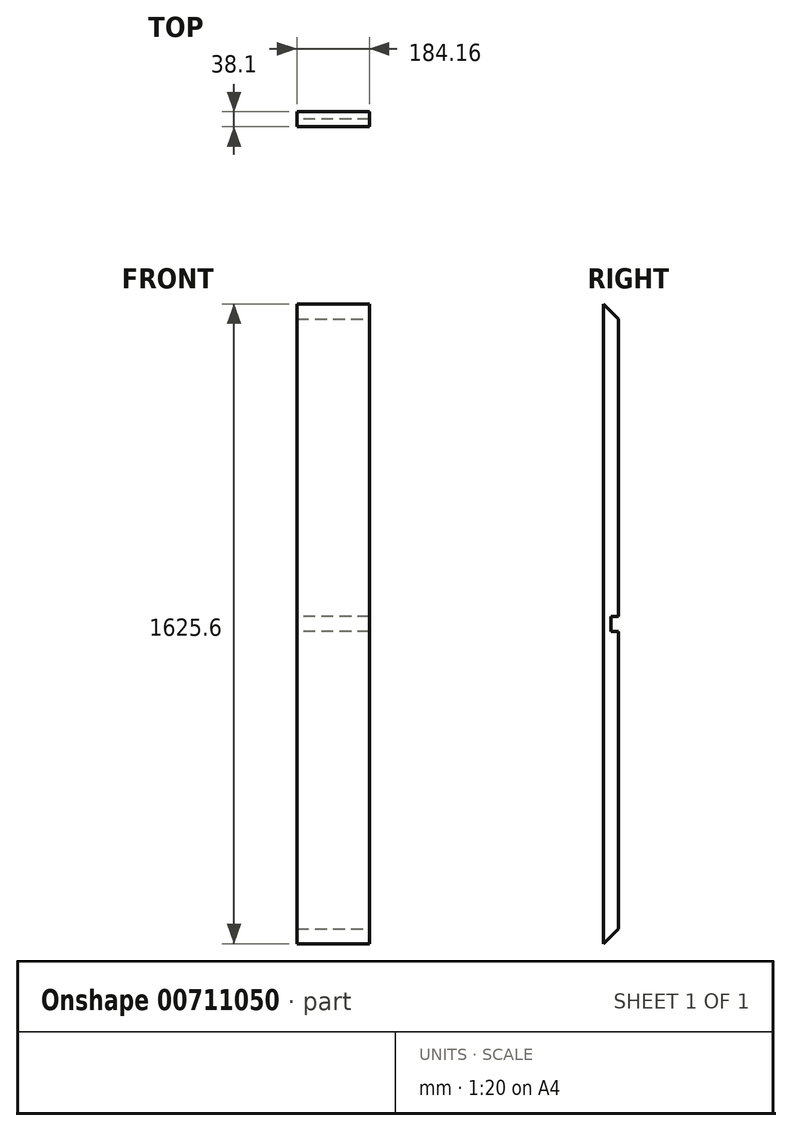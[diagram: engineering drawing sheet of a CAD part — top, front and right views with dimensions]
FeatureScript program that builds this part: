
annotation { "Feature Type Name" : "Feature", "Feature Type Description" : "" }
export const myFeature = defineFeature(function(context is Context, id is Id, definition is map)
    precondition{}
    {
        {
            var Q0;
            Q0=qCreatedBy(makeId("Top.planeOp"),FACE);
            var sketch = newSketch(context, id + "F0", { "sketchPlane" : qUnion([Q0])});
            skLineSegment(sketch, "E0.bottom", {"start": v(92.08, 19.05) * mm, "end": v(-92.08, 19.05) * mm});
            skLineSegment(sketch, "E0.top", {"start": v(92.08, -19.05) * mm, "end": v(-92.07, -19.05) * mm});
            skLineSegment(sketch, "E0.left", {"start": v(92.08, 19.05) * mm, "end": v(92.08, -19.05) * mm});
            skLineSegment(sketch, "E0.right", {"start": v(-92.08, 19.05) * mm, "end": v(-92.08, -19.05) * mm});
            skPoint(sketch, "E0.middle", {"position": v(0, 0) * mm});
            skSolve(sketch);
        }
        {
            var Q0;
            Q0=makeQuery(id+"F0.imprint","IMPRINT",FACE,{"disambiguationData":[TD([[makeQuery(id+"F0.imprint","IMPRINT",EDGE,{"derivedFrom":sQuery(id+"F0.wireOp",EDGE,"E0.bottom")}),1.0]])]});
            extrude(context, id + "F1", {"entities" : qUnion([Q0]), "depth" : 1625.6 * mm, "offsetDistance" : 25.4 * mm});
        }
        {
            var Q0;
            Q0=makeQuery(id+"F1.opExtrude","SWEPT_FACE",FACE,{"disambiguationData":[OSD([sQuery(id+"F0.wireOp",EDGE,"E0.left")])]});
            var sketch = newSketch(context, id + "F2", { "sketchPlane" : qUnion([Q0])});
            skLineSegment(sketch, "E1", {"start": v(-19.05, 1625.6) * mm, "end": v(19.05, 1587.5) * mm});
            skLineSegment(sketch, "E2", {"start": v(-19.05, 1625.6) * mm, "end": v(19.05, 1625.6) * mm});
            skLineSegment(sketch, "E3", {"start": v(19.05, 1625.6) * mm, "end": v(19.05, 1587.5) * mm});
            skLineSegment(sketch, "E4", {"start": v(-19.05, 0) * mm, "end": v(19.05, 38.1) * mm});
            skLineSegment(sketch, "E5", {"start": v(-19.05, 0) * mm, "end": v(19.05, 0) * mm});
            skLineSegment(sketch, "E6", {"start": v(19.05, 0) * mm, "end": v(19.05, 38.1) * mm});
            skSolve(sketch);
        }
        {
            var Q0;
            Q0 = qSketchRegion(id + "F2", true);
            extrude(context, id + "F3", {"entities" : qUnion([Q0]), "operationType" : NewBodyOperationType.REMOVE, "oppositeDirection" : true, "depth" : 190.5 * mm, "offsetDistance" : 25.4 * mm});
        }
        {
            var Q0;
            Q0=makeQuery(id+"F1.opExtrude","SWEPT_FACE",FACE,{"disambiguationData":[OSD([sQuery(id+"F0.wireOp",EDGE,"E0.bottom")])]});
            var sketch = newSketch(context, id + "F4", { "sketchPlane" : qUnion([Q0])});
            skLineSegment(sketch, "E7.0", {"start": v(-92.07, 793.75) * mm, "end": v(92.08, 793.75) * mm});
            skLineSegment(sketch, "E8.0", {"start": v(-92.08, 831.85) * mm, "end": v(92.08, 831.85) * mm});
            skLineSegment(sketch, "E9", {"start": v(-92.08, 831.85) * mm, "end": v(-92.07, 793.75) * mm});
            skLineSegment(sketch, "E10", {"start": v(92.07, 831.85) * mm, "end": v(92.08, 793.75) * mm});
            skSolve(sketch);
        }
        {
            var Q0;
            Q0 = qSketchRegion(id + "F4", true);
            extrude(context, id + "F5", {"entities" : qUnion([Q0]), "operationType" : NewBodyOperationType.REMOVE, "oppositeDirection" : true, "depth" : 19.05 * mm, "offsetDistance" : 25.4 * mm});
        }
    });
